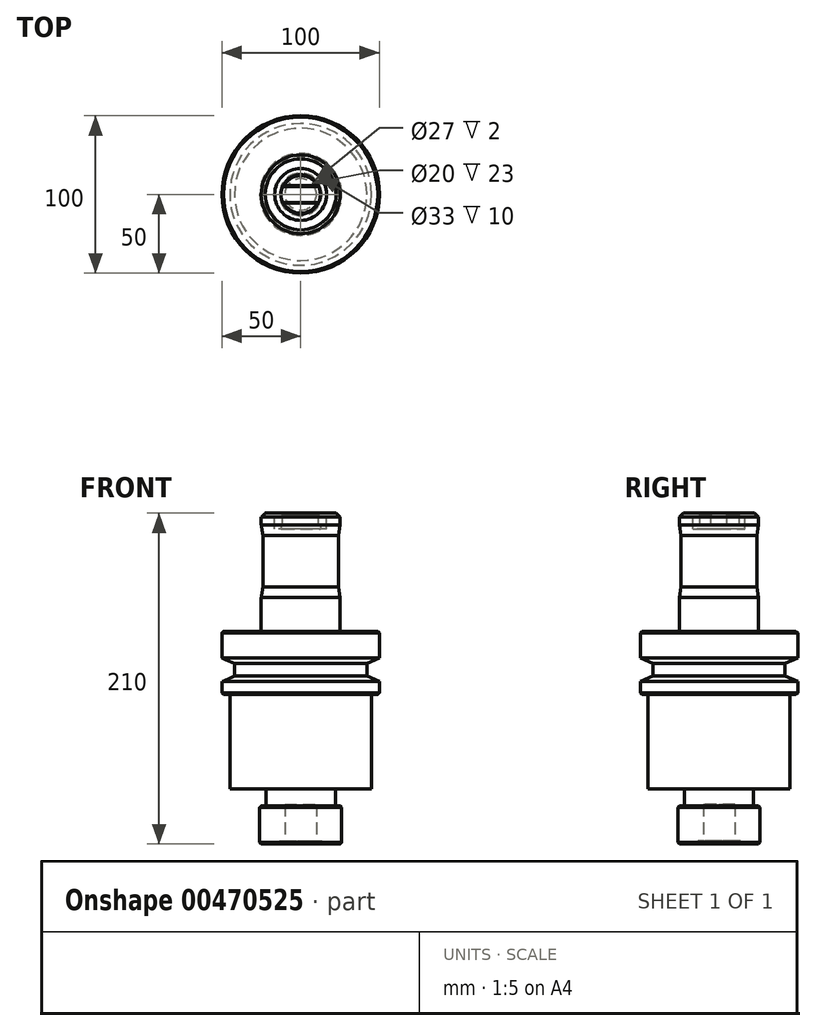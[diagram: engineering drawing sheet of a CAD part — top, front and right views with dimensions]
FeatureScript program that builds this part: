
annotation { "Feature Type Name" : "Feature", "Feature Type Description" : "" }
export const myFeature = defineFeature(function(context is Context, id is Id, definition is map)
    precondition{}
    {
        {
            var Q0;
            Q0=qCreatedBy(makeId("Front.planeOp"),FACE);
            var sketch = newSketch(context, id + "F0", { "sketchPlane" : qUnion([Q0])});
            skLineSegment(sketch, "E0", {"start": v(0, 0) * mm, "end": v(0, 210) * mm});
            skLineSegment(sketch, "E1", {"start": v(0, 210) * mm, "end": v(22.5, 210) * mm});
            skLineSegment(sketch, "E2", {"start": v(22.5, 210) * mm, "end": v(25, 207.5) * mm});
            skLineSegment(sketch, "E3", {"start": v(25, 207.5) * mm, "end": v(25, 202.5) * mm});
            skLineSegment(sketch, "E4", {"start": v(25, 202.5) * mm, "end": v(24, 196) * mm});
            skLineSegment(sketch, "E5", {"start": v(24, 196) * mm, "end": v(24, 163) * mm});
            skLineSegment(sketch, "E6", {"start": v(24, 163) * mm, "end": v(25, 156.5) * mm});
            skLineSegment(sketch, "E7", {"start": v(25, 156.5) * mm, "end": v(25, 135) * mm});
            skLineSegment(sketch, "E8", {"start": v(50, 118) * mm, "end": v(42, 114.5) * mm});
            skLineSegment(sketch, "E9", {"start": v(42, 114.5) * mm, "end": v(42, 106.5) * mm});
            skLineSegment(sketch, "E10", {"start": v(42, 106.5) * mm, "end": v(50, 103) * mm});
            skLineSegment(sketch, "E11", {"start": v(50, 103) * mm, "end": v(50, 95) * mm});
            skLineSegment(sketch, "E12", {"start": v(45, 95) * mm, "end": v(45, 35) * mm});
            skLineSegment(sketch, "E13", {"start": v(45, 35) * mm, "end": v(22, 35) * mm});
            skLineSegment(sketch, "E14", {"start": v(22, 35) * mm, "end": v(22, 24) * mm});
            skLineSegment(sketch, "E15", {"start": v(22, 24) * mm, "end": v(26, 24) * mm});
            skLineSegment(sketch, "E16", {"start": v(26, 24) * mm, "end": v(26, 0) * mm});
            skLineSegment(sketch, "E17", {"start": v(26, 0) * mm, "end": v(0, 0) * mm});
            skLineSegment(sketch, "E18", {"start": v(50, 95) * mm, "end": v(45, 95) * mm});
            skLineSegment(sketch, "E19", {"start": v(49, 135) * mm, "end": v(50, 134) * mm});
            skLineSegment(sketch, "E20", {"start": v(25, 135) * mm, "end": v(49, 135) * mm});
            skLineSegment(sketch, "E21", {"start": v(50, 134) * mm, "end": v(50, 118) * mm});
            skSolve(sketch);
        }
        {
            var Q0;
            Q0=makeQuery(id+"F0.imprint","IMPRINT",FACE,{"disambiguationData":[TD([[makeQuery(id+"F0.imprint","IMPRINT",EDGE,{"derivedFrom":sQuery(id+"F0.wireOp",EDGE,"E0")}),-1.0]])]});
            var Q1;
            Q1=sQuery(id+"F0.wireOp",EDGE,"E0");
            revolve(context, id + "F1", {"entities" : qUnion([Q0]), "axis" : qUnion([Q1]), "revolveType" : RevolveType.FULL});
        }
        {
            var Q0;
            Q0=makeQuery(id+"F1.opRevolve","SWEPT_FACE",FACE,{"disambiguationData":[OSD([sQuery(id+"F0.wireOp",EDGE,"E17")])]});
            var sketch = newSketch(context, id + "F2", { "sketchPlane" : qUnion([Q0])});
            skCircle(sketch, "E22", {"center": v(0, 0) * mm, "radius": 10 * mm});
            skCircle(sketch, "E23", {"center": v(0, 0) * mm, "radius": 13.5 * mm});
            skSolve(sketch);
        }
        {
            var Q0;
            Q0=makeQuery(id+"F2.imprint","IMPRINT",FACE,{"disambiguationData":[TD([[makeQuery(id+"F2.imprint","IMPRINT",EDGE,{"derivedFrom":sQuery(id+"F2.wireOp",EDGE,"E22")}),-1.0]])]});
            extrude(context, id + "F3", {"entities" : qUnion([Q0]), "operationType" : NewBodyOperationType.REMOVE, "oppositeDirection" : true, "depth" : 2 * mm});
        }
        {
            var Q0;
            Q0=makeQuery(id+"F2.imprint","IMPRINT",FACE,{"disambiguationData":[TD([[makeQuery(id+"F2.imprint","IMPRINT",EDGE,{"derivedFrom":sQuery(id+"F2.wireOp",EDGE,"E22")}),1.0]])]});
            extrude(context, id + "F4", {"entities" : qUnion([Q0]), "operationType" : NewBodyOperationType.REMOVE, "oppositeDirection" : true, "depth" : 25 * mm});
        }
        {
            var Q0;
            Q0=makeQuery(id+"F1.opRevolve","SWEPT_FACE",FACE,{"disambiguationData":[OSD([sQuery(id+"F0.wireOp",EDGE,"E1")])]});
            var sketch = newSketch(context, id + "F5", { "sketchPlane" : qUnion([Q0])});
            skCircle(sketch, "E24", {"center": v(0, 0) * mm, "radius": 16.5 * mm});
            skSolve(sketch);
        }
        {
            var Q0;
            Q0=makeQuery(id+"F5.imprint","IMPRINT",FACE,{"disambiguationData":[TD([[makeQuery(id+"F5.imprint","IMPRINT",EDGE,{"derivedFrom":sQuery(id+"F5.wireOp",EDGE,"E24")}),1.0]])]});
            extrude(context, id + "F6", {"entities" : qUnion([Q0]), "operationType" : NewBodyOperationType.REMOVE, "oppositeDirection" : true, "depth" : 10 * mm});
        }
        {
            var Q0;
            Q0=makeQuery(id+"F6.boolean.opBoolean","COPY",FACE,{"derivedFrom":makeQuery(id+"F6.opExtrude","CAP_FACE",FACE,{"disambiguationData":[OSD([sQuery(id+"F5.wireOp",EDGE,"E24")])],"isStart":false})});
            var sketch = newSketch(context, id + "F7", { "sketchPlane" : qUnion([Q0])});
            skCircle(sketch, "E25", {"center": v(0, 0) * mm, "radius": 12.5 * mm});
            skSolve(sketch);
        }
        {
            var Q0;
            Q0=makeQuery(id+"F7.imprint","IMPRINT",FACE,{"disambiguationData":[TD([[makeQuery(id+"F7.imprint","IMPRINT",EDGE,{"derivedFrom":sQuery(id+"F7.wireOp",EDGE,"E25")}),1.0]])]});
            extrude(context, id + "F8", {"entities" : qUnion([Q0]), "operationType" : NewBodyOperationType.ADD, "depth" : 9.5 * mm});
        }
        {
            var Q0;
            Q0=makeQuery(id+"F8.opExtrude","CAP_FACE",FACE,{"disambiguationData":[OSD([sQuery(id+"F7.wireOp",EDGE,"E25")])],"isStart":false});
            var sketch = newSketch(context, id + "F9", { "sketchPlane" : qUnion([Q0])});
            skLineSegment(sketch, "E26.bottom", {"start": v(13, 5.05) * mm, "end": v(-13, 5.05) * mm});
            skLineSegment(sketch, "E26.top", {"start": v(13, -5.05) * mm, "end": v(-13, -5.05) * mm});
            skLineSegment(sketch, "E26.left", {"start": v(13, 5.05) * mm, "end": v(13, -5.05) * mm});
            skLineSegment(sketch, "E26.right", {"start": v(-13, 5.05) * mm, "end": v(-13, -5.05) * mm});
            skSolve(sketch);
        }
        {
            var Q0;
            {var subQ0=sQuery(id+"F9.wireOp",EDGE,"E26.bottom");var subQ1=makeQuery(id+"F8.opExtrude","CAP_EDGE",EDGE,{"disambiguationData":[OSD([sQuery(id+"F7.wireOp",EDGE,"E25")])],"isStart":false});var subQ2=makeQuery(id+"F9.imprint","INTERSECT",VERTEX,{"disambiguationData":[OD(0.0)],"derivedFrom":[subQ1,subQ0]});Q0=makeQuery(id+"F9.imprint","IMPRINT",FACE,{"disambiguationData":[TD([[makeQuery(id+"F9.imprint","IMPRINT",EDGE,{"disambiguationData":[TD([[subQ2,-1.0]])],"derivedFrom":subQ0}),1.0]])]});}
            extrude(context, id + "F10", {"entities" : qUnion([Q0]), "operationType" : NewBodyOperationType.REMOVE, "oppositeDirection" : true, "depth" : 7 * mm});
        }
        {
            var Q0;
            {var subQ0=sQuery(id+"F7.wireOp",EDGE,"E25");Q0=makeQuery(id+"F10.boolean.opBoolean","SPLIT",FACE,{"disambiguationData":[TD([makeQuery(id+"F10.opExtrude","SWEPT_FACE",FACE,{"disambiguationData":[OSD([sQuery(id+"F9.wireOp",EDGE,"E26.bottom")])]})])],"derivedFrom":makeQuery(id+"F8.opExtrude","CAP_FACE",FACE,{"disambiguationData":[OSD([subQ0])],"isStart":false})});}
            var Q1;
            {var subQ0=sQuery(id+"F7.wireOp",EDGE,"E25");Q1=makeQuery(id+"F10.boolean.opBoolean","SPLIT",FACE,{"disambiguationData":[TD([makeQuery(id+"F10.opExtrude","SWEPT_FACE",FACE,{"disambiguationData":[OSD([sQuery(id+"F9.wireOp",EDGE,"E26.top")])]})])],"derivedFrom":makeQuery(id+"F8.opExtrude","CAP_FACE",FACE,{"disambiguationData":[OSD([subQ0])],"isStart":false})});}
            chamfer(context, id + "F11", {"entities" : qUnion([Q0, Q1]), "width" : 0.5 * mm, "tangentPropagation" : true});
        }
        {
            var Q0;
            Q0=makeQuery(id+"F1.opRevolve","SWEPT_EDGE",EDGE,{"disambiguationData":[OSD([sQuery(id+"F0.wireOp",EDGE,"E11"),sQuery(id+"F0.wireOp",EDGE,"E18")])]});
            chamfer(context, id + "F12", {"entities" : qUnion([Q0]), "width" : 1 * mm, "tangentPropagation" : true});
        }
        {
            var Q0;
            Q0=makeQuery(id+"F1.opRevolve","SWEPT_EDGE",EDGE,{"disambiguationData":[OSD([sQuery(id+"F0.wireOp",EDGE,"E15"),sQuery(id+"F0.wireOp",EDGE,"E16")])]});
            var Q1;
            Q1=makeQuery(id+"F1.opRevolve","SWEPT_EDGE",EDGE,{"disambiguationData":[OSD([sQuery(id+"F0.wireOp",EDGE,"E16"),sQuery(id+"F0.wireOp",EDGE,"E17")])]});
            chamfer(context, id + "F13", {"entities" : qUnion([Q0, Q1]), "width" : 0.8 * mm, "tangentPropagation" : true});
        }
    });
